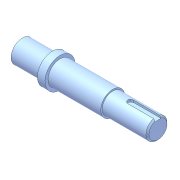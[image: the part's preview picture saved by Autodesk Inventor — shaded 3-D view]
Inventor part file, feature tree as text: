
AUTODESK INVENTOR PART (.ipt)
format: ipt  version: unknown  size: 200,192 bytes
history: native  units: in
note: dims shown in document units (in); Inventor stores cm internally (conversion verified against a paired STEP export)
features: sketch x2, revolve x1, chamfer x1, extrude x1, fillet x1
ambient origin geometry x8: Origin, YZ Plane, XZ Plane, XY Plane, X Axis, Y Axis, Z Axis, Center Point
feature tree (6):
  revolve  "Revolution4"  [1 undecoded]
  chamfer  "Chamfer3"  Distance=0.315in
  extrude  "Extrusion5"  Depth=0.2756in
  fillet  "Fillet4"  Radius=0.7874in
  sketch  "Sketch8"  dims[d2=0.2756in d55=0.2953in]
  sketch  "Sketch9"  dims[d56=0.3937in d57=0.315in d58=0.2756in d59=0.7874in d60=0.1969in d61=1.1811in d62=1.378in d63=90.0deg d64=0.0394in d65=0.0787in d66=45.0deg d67=0.2087in d68=0.1575in d69=0.0787in d70=0.7874in d71=0.0in d72=0.0787in]
note: 1 required parameter value undecoded (feature->parameter linkage not recoverable at this tier; creation-order binding heuristic only, values carry confidence <= 0.55)
